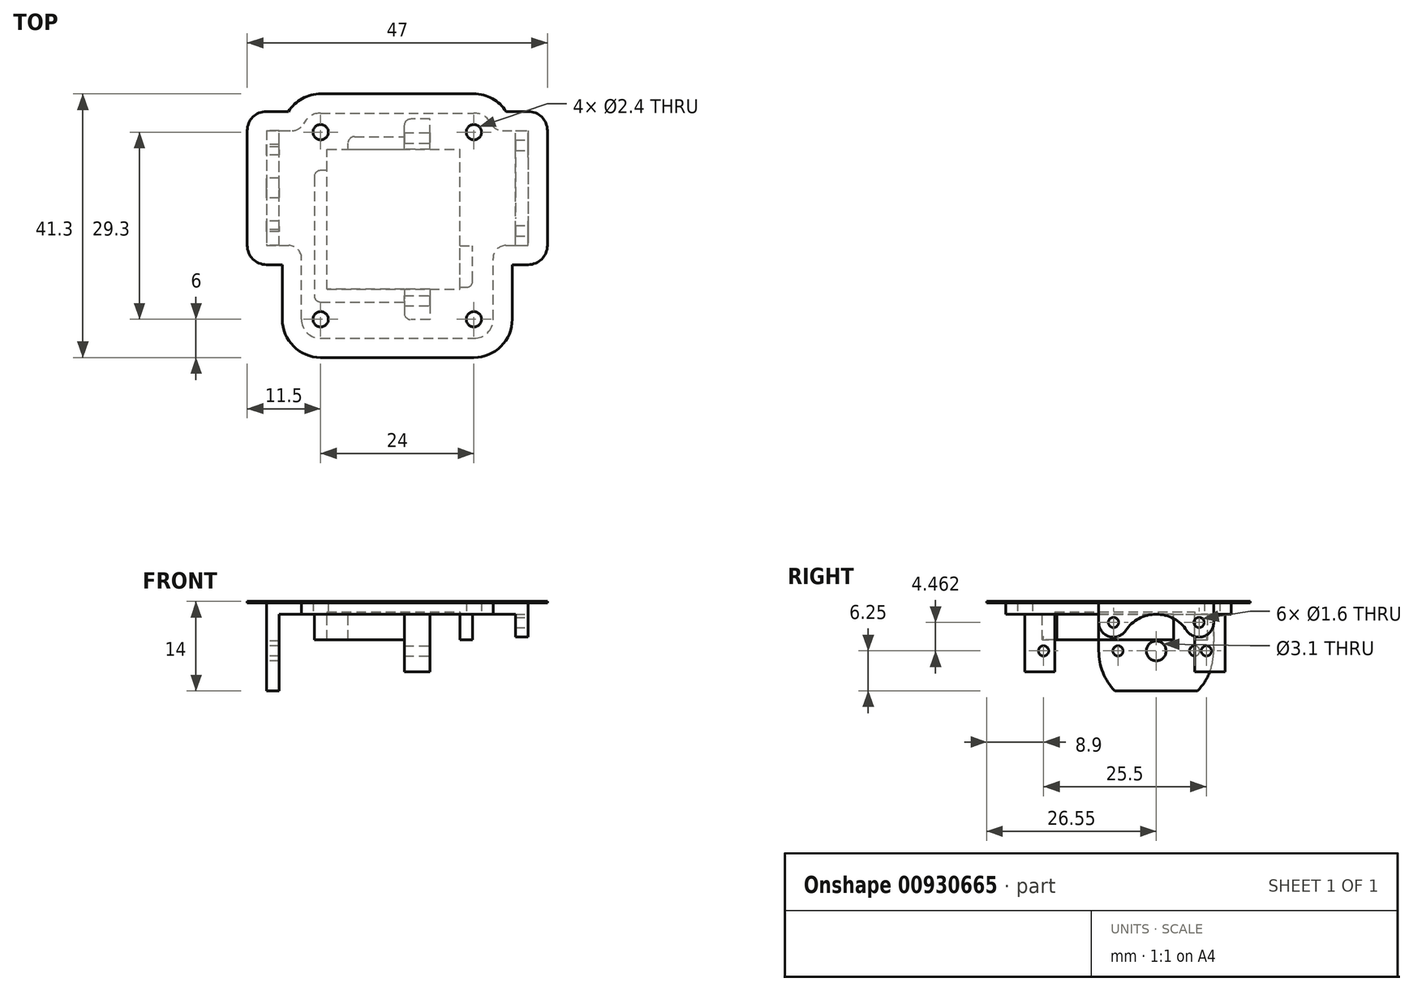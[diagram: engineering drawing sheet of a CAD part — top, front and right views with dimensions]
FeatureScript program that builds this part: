
annotation { "Feature Type Name" : "Feature", "Feature Type Description" : "" }
export const myFeature = defineFeature(function(context is Context, id is Id, definition is map)
    precondition{}
    {
        {
            var Q0;
            Q0=qCreatedBy(makeId("Top.planeOp"),FACE);
            var sketch = newSketch(context, id + "F0", { "sketchPlane" : qUnion([Q0])});
            skLineSegment(sketch, "E0.bottom", {"start": v(0, 0) * mm, "end": v(15.8, 0) * mm, "construction": true});
            skLineSegment(sketch, "E0.top", {"start": v(3, 21.3) * mm, "end": v(15.8, 21.3) * mm, "construction": true});
            skLineSegment(sketch, "E0.left", {"start": v(0, 0) * mm, "end": v(0, 18.3) * mm, "construction": true});
            skLineSegment(sketch, "E0.right", {"start": v(20.2, 0) * mm, "end": v(20.2, 21.3) * mm, "construction": true});
            skLineSegment(sketch, "E1.bottom", {"start": v(16.5, 25.35) * mm, "end": v(15.8, 25.35) * mm, "construction": true});
            skLineSegment(sketch, "E1.top", {"start": v(16.5, -4.05) * mm, "end": v(15.8, -4.05) * mm, "construction": true});
            skLineSegment(sketch, "E1.left", {"start": v(16.5, 25.35) * mm, "end": v(16.5, 21.3) * mm, "construction": true});
            skLineSegment(sketch, "E1.right", {"start": v(15.8, 25.35) * mm, "end": v(15.8, 21.3) * mm, "construction": true});
            skLineSegment(sketch, "E2.trimOffspring", {"start": v(16.5, 21.3) * mm, "end": v(20.2, 21.3) * mm, "construction": true});
            skLineSegment(sketch, "E3.trimOffspring", {"start": v(15.8, 0) * mm, "end": v(15.8, -4.05) * mm, "construction": true});
            skLineSegment(sketch, "E4.trimOffspring", {"start": v(16.5, 0) * mm, "end": v(16.5, -4.05) * mm, "construction": true});
            skLineSegment(sketch, "E5.trimOffspring", {"start": v(16.5, 0) * mm, "end": v(20.2, 0) * mm, "construction": true});
            skLineSegment(sketch, "E6", {"start": v(15.8, 23.4) * mm, "end": v(16.5, 23.4) * mm, "construction": true});
            skLineSegment(sketch, "E7", {"start": v(15.8, -2.1) * mm, "end": v(16.5, -2.1) * mm, "construction": true});
            skLineSegment(sketch, "E8", {"start": v(0, 18.3) * mm, "end": v(3, 21.3) * mm, "construction": true});
            skPoint(sketch, "E9.orphan", {"position": v(0, 21.3) * mm});
            skLineSegment(sketch, "E10", {"start": v(20.2, 21.3) * mm, "end": v(24.2, 21.3) * mm, "construction": true});
            skLineSegment(sketch, "E11", {"start": v(24.2, 21.3) * mm, "end": v(24.2, 6.8) * mm, "construction": true});
            skLineSegment(sketch, "E12", {"start": v(24.2, 6.8) * mm, "end": v(20.2, 6.8) * mm, "construction": true});
            skLineSegment(sketch, "E13", {"start": v(24.2, 15.55) * mm, "end": v(28.7, 15.55) * mm, "construction": true});
            skLineSegment(sketch, "E14.bottom", {"start": v(28.7, 21.3) * mm, "end": v(26.7, 21.3) * mm, "construction": true});
            skLineSegment(sketch, "E14.top", {"start": v(28.7, 0) * mm, "end": v(26.7, 0) * mm, "construction": true});
            skLineSegment(sketch, "E14.left", {"start": v(28.7, 21.3) * mm, "end": v(28.7, 0) * mm, "construction": true});
            skLineSegment(sketch, "E14.right", {"start": v(26.7, 21.3) * mm, "end": v(26.7, 0) * mm, "construction": true});
            skLineSegment(sketch, "E15.bottom", {"start": v(-7.3, 21.3) * mm, "end": v(-5.3, 21.3) * mm, "construction": true});
            skLineSegment(sketch, "E15.top", {"start": v(-7.3, 0) * mm, "end": v(-5.3, 0) * mm, "construction": true});
            skLineSegment(sketch, "E15.left", {"start": v(-7.3, 21.3) * mm, "end": v(-7.3, 0) * mm, "construction": true});
            skLineSegment(sketch, "E15.right", {"start": v(-5.3, 21.3) * mm, "end": v(-5.3, 0) * mm, "construction": true});
            skLineSegment(sketch, "E16", {"start": v(24.2, 18.55) * mm, "end": v(26.7, 18.55) * mm, "construction": true});
            skLineSegment(sketch, "E17", {"start": v(24.2, 12.55) * mm, "end": v(26.7, 12.55) * mm, "construction": true});
            skSolve(sketch);
        }
        {
            var Q0;
            Q0=qCreatedBy(makeId("Top.planeOp"),FACE);
            var sketch = newSketch(context, id + "F1", { "sketchPlane" : qUnion([Q0])});
            skLineSegment(sketch, "E18.left", {"start": v(-9.8, 24.55) * mm, "end": v(-9.8, 6.55) * mm});
            skLineSegment(sketch, "E18.right", {"start": v(31.2, 24.55) * mm, "end": v(31.2, 6.55) * mm});
            skLineSegment(sketch, "E19", {"start": v(10.7, 27.3) * mm, "end": v(10.7, -8) * mm, "construction": true});
            skCircle(sketch, "E20", {"center": v(-1.3, 24.3) * mm, "radius": 1.2 * mm});
            skCircle(sketch, "E21", {"center": v(22.7, 24.3) * mm, "radius": 1.2 * mm});
            skCircle(sketch, "E22", {"center": v(-1.3, -5) * mm, "radius": 1.2 * mm});
            skCircle(sketch, "E23", {"center": v(22.7, -5) * mm, "radius": 1.2 * mm});
            skLineSegment(sketch, "E24", {"start": v(-1.3, 24.3) * mm, "end": v(22.7, 24.3) * mm, "construction": true});
            skLineSegment(sketch, "E25", {"start": v(-1.3, 24.3) * mm, "end": v(-1.3, -5) * mm, "construction": true});
            skLineSegment(sketch, "E26", {"start": v(-1.3, -5) * mm, "end": v(22.7, -5) * mm, "construction": true});
            skLineSegment(sketch, "E27", {"start": v(22.7, -5) * mm, "end": v(22.7, 24.3) * mm, "construction": true});
            skArc(sketch, "E28", {"start": v(-1.3, 27.3) * mm, "mid": v(-3.33, 26.5) * mm, "end": v(-4.29, 24.55) * mm});
            skArc(sketch, "E29", {"start": v(25.69, 24.55) * mm, "mid": v(24.73, 26.5) * mm, "end": v(22.7, 27.3) * mm});
            skArc(sketch, "E30", {"start": v(-4.3, -5) * mm, "mid": v(-3.42, -7.12) * mm, "end": v(-1.3, -8) * mm});
            skArc(sketch, "E31", {"start": v(22.7, -8) * mm, "mid": v(24.82, -7.12) * mm, "end": v(25.7, -5) * mm});
            skLineSegment(sketch, "E32", {"start": v(-1.3, 27.3) * mm, "end": v(22.7, 27.3) * mm});
            skLineSegment(sketch, "E33", {"start": v(-4.3, -5) * mm, "end": v(-4.3, 6.55) * mm});
            skLineSegment(sketch, "E34", {"start": v(25.7, -5) * mm, "end": v(25.7, 6.55) * mm});
            skLineSegment(sketch, "E35", {"start": v(-1.3, -8) * mm, "end": v(22.7, -8) * mm});
            skLineSegment(sketch, "E36", {"start": v(-9.8, 24.55) * mm, "end": v(-4.29, 24.55) * mm});
            skLineSegment(sketch, "E37", {"start": v(25.69, 24.55) * mm, "end": v(31.2, 24.55) * mm});
            skLineSegment(sketch, "E38", {"start": v(-9.8, 6.55) * mm, "end": v(-4.3, 6.55) * mm});
            skLineSegment(sketch, "E39", {"start": v(25.7, 6.55) * mm, "end": v(31.2, 6.55) * mm});
            skSolve(sketch);
        }
        {
            var Q0;
            Q0=qSketchRegion(id+"F1",true);
            extrude(context, id + "F2", {"entities" : qUnion([Q0]), "depth" : 2 * mm, "offsetDistance" : 25 * mm});
        }
        {
            var Q0;
            Q0=makeQuery(id+"F2.opExtrude","SWEPT_EDGE",EDGE,{"disambiguationData":[OSD([sQuery(id+"F1.wireOp",EDGE,"E18.bottom"),sQuery(id+"F1.wireOp",EDGE,"n9spz6sa-SeqF-ro3C-UlOU-JdgqFO8XuwJj")])]});
            var Q1;
            Q1=makeQuery(id+"F2.opExtrude","SWEPT_EDGE",EDGE,{"disambiguationData":[OSD([sQuery(id+"F1.wireOp",EDGE,"v9wraEXt-J1L3-XLAm-fg3X-uzmLA6GDD1Q5"),sQuery(id+"F1.wireOp",EDGE,"3bf1b7fd-33ad-4c0a-b081-5d8ae0c3909f.trimOffspring")])]});
            var Q2;
            Q2=makeQuery(id+"F2.opExtrude","SWEPT_EDGE",EDGE,{"disambiguationData":[OSD([sQuery(id+"F1.wireOp",EDGE,"E34"),sQuery(id+"F1.wireOp",EDGE,"87065f72-439b-48f6-8dea-1321e7ddb749.trimOffspring")])]});
            var Q3;
            Q3=makeQuery(id+"F2.opExtrude","SWEPT_EDGE",EDGE,{"disambiguationData":[OSD([sQuery(id+"F1.wireOp",EDGE,"E18.top"),sQuery(id+"F1.wireOp",EDGE,"E33")])]});
            fillet(context, id + "F3", {"entities" : qUnion([Q0, Q1, Q2, Q3]), "radius" : 2 * mm, "tangentPropagation" : true, "allowEdgeOverflow" : false});
        }
        {
            var Q0;
            Q0=makeQuery(id+"F2.opExtrude","CAP_FACE",FACE,{"disambiguationData":[OSD([sQuery(id+"F1.wireOp",EDGE,"E18.bottom"),sQuery(id+"F1.wireOp",EDGE,"E18.top"),sQuery(id+"F1.wireOp",EDGE,"E18.left"),sQuery(id+"F1.wireOp",EDGE,"E18.right"),sQuery(id+"F1.wireOp",EDGE,"E20"),sQuery(id+"F1.wireOp",EDGE,"E21"),sQuery(id+"F1.wireOp",EDGE,"E22"),sQuery(id+"F1.wireOp",EDGE,"E23"),sQuery(id+"F1.wireOp",EDGE,"E28"),sQuery(id+"F1.wireOp",EDGE,"E29"),sQuery(id+"F1.wireOp",EDGE,"E30"),sQuery(id+"F1.wireOp",EDGE,"E31"),sQuery(id+"F1.wireOp",EDGE,"n9spz6sa-SeqF-ro3C-UlOU-JdgqFO8XuwJj"),sQuery(id+"F1.wireOp",EDGE,"E32"),sQuery(id+"F1.wireOp",EDGE,"v9wraEXt-J1L3-XLAm-fg3X-uzmLA6GDD1Q5"),sQuery(id+"F1.wireOp",EDGE,"E33"),sQuery(id+"F1.wireOp",EDGE,"E34"),sQuery(id+"F1.wireOp",EDGE,"E35"),sQuery(id+"F1.wireOp",EDGE,"3bf1b7fd-33ad-4c0a-b081-5d8ae0c3909f.trimOffspring"),sQuery(id+"F1.wireOp",EDGE,"87065f72-439b-48f6-8dea-1321e7ddb749.trimOffspring")])],"isStart":true});
            var sketch = newSketch(context, id + "F4", { "sketchPlane" : qUnion([Q0])});
            skLineSegment(sketch, "E40.bottom", {"start": v(15.8, 0.3) * mm, "end": v(11.8, 0.3) * mm});
            skLineSegment(sketch, "E40.top", {"start": v(15.8, 5.05) * mm, "end": v(11.8, 5.05) * mm});
            skLineSegment(sketch, "E40.left", {"start": v(15.8, 0.3) * mm, "end": v(15.8, 5.05) * mm});
            skLineSegment(sketch, "E40.right", {"start": v(11.8, 0.3) * mm, "end": v(11.8, 5.05) * mm});
            skLineSegment(sketch, "E41.bottom", {"start": v(15.8, -21.6) * mm, "end": v(11.8, -21.6) * mm});
            skLineSegment(sketch, "E41.top", {"start": v(15.8, -26.35) * mm, "end": v(11.8, -26.35) * mm});
            skLineSegment(sketch, "E41.left", {"start": v(15.8, -21.6) * mm, "end": v(15.8, -26.35) * mm});
            skLineSegment(sketch, "E41.right", {"start": v(11.8, -21.6) * mm, "end": v(11.8, -26.35) * mm});
            skSolve(sketch);
        }
        {
            var Q0;
            Q0=qSketchRegion(id+"F4",true);
            extrude(context, id + "F5", {"entities" : qUnion([Q0]), "operationType" : NewBodyOperationType.ADD, "depth" : 9 * mm, "offsetDistance" : 25 * mm});
        }
        {
            var Q0;
            Q0=makeQuery(id+"F2.opExtrude","CAP_FACE",FACE,{"disambiguationData":[OSD([sQuery(id+"F1.wireOp",EDGE,"E18.bottom"),sQuery(id+"F1.wireOp",EDGE,"E18.top"),sQuery(id+"F1.wireOp",EDGE,"E18.left"),sQuery(id+"F1.wireOp",EDGE,"E18.right"),sQuery(id+"F1.wireOp",EDGE,"E20"),sQuery(id+"F1.wireOp",EDGE,"E21"),sQuery(id+"F1.wireOp",EDGE,"E22"),sQuery(id+"F1.wireOp",EDGE,"E23"),sQuery(id+"F1.wireOp",EDGE,"E28"),sQuery(id+"F1.wireOp",EDGE,"E29"),sQuery(id+"F1.wireOp",EDGE,"E30"),sQuery(id+"F1.wireOp",EDGE,"E31"),sQuery(id+"F1.wireOp",EDGE,"n9spz6sa-SeqF-ro3C-UlOU-JdgqFO8XuwJj"),sQuery(id+"F1.wireOp",EDGE,"E32"),sQuery(id+"F1.wireOp",EDGE,"v9wraEXt-J1L3-XLAm-fg3X-uzmLA6GDD1Q5"),sQuery(id+"F1.wireOp",EDGE,"E33"),sQuery(id+"F1.wireOp",EDGE,"E34"),sQuery(id+"F1.wireOp",EDGE,"E35"),sQuery(id+"F1.wireOp",EDGE,"3bf1b7fd-33ad-4c0a-b081-5d8ae0c3909f.trimOffspring"),sQuery(id+"F1.wireOp",EDGE,"87065f72-439b-48f6-8dea-1321e7ddb749.trimOffspring")])],"isStart":true});
            var sketch = newSketch(context, id + "F6", { "sketchPlane" : qUnion([Q0])});
            skLineSegment(sketch, "E42", {"start": v(-0.3, -18.3) * mm, "end": v(-2.3, -18.3) * mm});
            skLineSegment(sketch, "E43", {"start": v(-2.3, -18.3) * mm, "end": v(-2.3, 2.3) * mm});
            skLineSegment(sketch, "E44", {"start": v(-2.3, 2.3) * mm, "end": v(11.8, 2.3) * mm});
            skLineSegment(sketch, "E45", {"start": v(11.8, 2.3) * mm, "end": v(11.8, 0.3) * mm});
            skLineSegment(sketch, "E46", {"start": v(11.8, 0.3) * mm, "end": v(-0.3, 0.3) * mm});
            skLineSegment(sketch, "E47", {"start": v(-0.3, 0.3) * mm, "end": v(-0.3, -18.3) * mm});
            skLineSegment(sketch, "E48.bottom", {"start": v(3, -21.6) * mm, "end": v(11.8, -21.6) * mm});
            skLineSegment(sketch, "E48.top", {"start": v(3, -23.6) * mm, "end": v(11.8, -23.6) * mm});
            skLineSegment(sketch, "E48.left", {"start": v(3, -21.6) * mm, "end": v(3, -23.6) * mm});
            skLineSegment(sketch, "E48.right", {"start": v(11.8, -21.6) * mm, "end": v(11.8, -23.6) * mm});
            skLineSegment(sketch, "E49.bottom", {"start": v(20.5, 0) * mm, "end": v(22.5, 0) * mm});
            skLineSegment(sketch, "E49.top", {"start": v(20.5, -6.5) * mm, "end": v(22.5, -6.5) * mm});
            skLineSegment(sketch, "E49.left", {"start": v(20.5, 0) * mm, "end": v(20.5, -6.5) * mm});
            skLineSegment(sketch, "E49.right", {"start": v(22.5, 0) * mm, "end": v(22.5, -6.5) * mm});
            skSolve(sketch);
        }
        {
            var Q0;
            Q0=qSketchRegion(id+"F6",true);
            extrude(context, id + "F7", {"entities" : qUnion([Q0]), "operationType" : NewBodyOperationType.ADD, "depth" : 4 * mm, "offsetDistance" : 25 * mm});
        }
        {
            var Q0;
            Q0=makeQuery(id+"F5.opExtrude","SWEPT_FACE",FACE,{"disambiguationData":[OSD([sQuery(id+"F4.wireOp",EDGE,"E41.left")])]});
            var sketch = newSketch(context, id + "F8", { "sketchPlane" : qUnion([Q0])});
            skCircle(sketch, "E50", {"center": v(23.4, -5.75) * mm, "radius": 0.8 * mm});
            skCircle(sketch, "E51", {"center": v(-2.1, -5.75) * mm, "radius": 0.8 * mm});
            skSolve(sketch);
        }
        {
            var Q0;
            Q0=qSketchRegion(id+"F8",true);
            extrude(context, id + "F9", {"entities" : qUnion([Q0]), "operationType" : NewBodyOperationType.REMOVE, "endBound" : BoundingType.UP_TO_NEXT, "oppositeDirection" : true, "depth" : 25 * mm, "offsetDistance" : 25 * mm});
        }
        {
            var Q0;
            Q0=makeQuery(id+"F7.opExtrude","CAP_EDGE",EDGE,{"disambiguationData":[OSD([sQuery(id+"F6.wireOp",EDGE,"E45")])],"isStart":false});
            var Q1;
            Q1=makeQuery(id+"F7.opExtrude","SWEPT_EDGE",EDGE,{"disambiguationData":[OSD([sQuery(id+"F4.wireOp",EDGE,"E40.right"),sQuery(id+"F6.wireOp",EDGE,"E44"),sQuery(id+"F6.wireOp",EDGE,"E45")])]});
            var Q2;
            Q2=makeQuery(id+"F7.opExtrude","SWEPT_EDGE",EDGE,{"disambiguationData":[OSD([sQuery(id+"F6.wireOp",EDGE,"E43"),sQuery(id+"F6.wireOp",EDGE,"E44")])]});
            var Q3;
            Q3=makeQuery(id+"F7.opExtrude","SWEPT_EDGE",EDGE,{"disambiguationData":[OSD([sQuery(id+"F6.wireOp",EDGE,"E42"),sQuery(id+"F6.wireOp",EDGE,"E43")])]});
            var Q4;
            Q4=makeQuery(id+"F7.opExtrude","SWEPT_EDGE",EDGE,{"disambiguationData":[OSD([sQuery(id+"F6.wireOp",EDGE,"E48.top"),sQuery(id+"F6.wireOp",EDGE,"E48.left")])]});
            var Q5;
            Q5=makeQuery(id+"F7.opExtrude","SWEPT_EDGE",EDGE,{"disambiguationData":[OSD([sQuery(id+"F4.wireOp",EDGE,"E41.right"),sQuery(id+"F6.wireOp",EDGE,"E48.top"),sQuery(id+"F6.wireOp",EDGE,"E48.right")])]});
            var Q6;
            Q6=makeQuery(id+"F7.opExtrude","CAP_EDGE",EDGE,{"disambiguationData":[OSD([sQuery(id+"F6.wireOp",EDGE,"E48.right")])],"isStart":false});
            var Q7;
            Q7=makeQuery(id+"F7.opExtrude","SWEPT_EDGE",EDGE,{"disambiguationData":[OSD([sQuery(id+"F6.wireOp",EDGE,"E49.bottom"),sQuery(id+"F6.wireOp",EDGE,"E49.right")])]});
            var Q8;
            Q8=makeQuery(id+"F5.opExtrude","SWEPT_EDGE",EDGE,{"disambiguationData":[OSD([sQuery(id+"F4.wireOp",EDGE,"E41.top"),sQuery(id+"F4.wireOp",EDGE,"E41.right")])]});
            var Q9;
            Q9=makeQuery(id+"F5.opExtrude","SWEPT_EDGE",EDGE,{"disambiguationData":[OSD([sQuery(id+"F4.wireOp",EDGE,"E40.top"),sQuery(id+"F4.wireOp",EDGE,"E40.right")])]});
            fillet(context, id + "F10", {"entities" : qUnion([Q0, Q1, Q2, Q3, Q4, Q5, Q6, Q7, Q8, Q9]), "radius" : 1 * mm, "tangentPropagation" : true, "allowEdgeOverflow" : false});
        }
        {
            var Q0;
            Q0=makeQuery(id+"F2.opExtrude","CAP_FACE",FACE,{"disambiguationData":[OSD([sQuery(id+"F1.wireOp",EDGE,"E18.bottom"),sQuery(id+"F1.wireOp",EDGE,"E18.top"),sQuery(id+"F1.wireOp",EDGE,"E18.left"),sQuery(id+"F1.wireOp",EDGE,"E18.right"),sQuery(id+"F1.wireOp",EDGE,"E20"),sQuery(id+"F1.wireOp",EDGE,"E21"),sQuery(id+"F1.wireOp",EDGE,"E22"),sQuery(id+"F1.wireOp",EDGE,"E23"),sQuery(id+"F1.wireOp",EDGE,"E28"),sQuery(id+"F1.wireOp",EDGE,"E29"),sQuery(id+"F1.wireOp",EDGE,"E30"),sQuery(id+"F1.wireOp",EDGE,"E31"),sQuery(id+"F1.wireOp",EDGE,"n9spz6sa-SeqF-ro3C-UlOU-JdgqFO8XuwJj"),sQuery(id+"F1.wireOp",EDGE,"E32"),sQuery(id+"F1.wireOp",EDGE,"v9wraEXt-J1L3-XLAm-fg3X-uzmLA6GDD1Q5"),sQuery(id+"F1.wireOp",EDGE,"E33"),sQuery(id+"F1.wireOp",EDGE,"E34"),sQuery(id+"F1.wireOp",EDGE,"E35"),sQuery(id+"F1.wireOp",EDGE,"3bf1b7fd-33ad-4c0a-b081-5d8ae0c3909f.trimOffspring"),sQuery(id+"F1.wireOp",EDGE,"87065f72-439b-48f6-8dea-1321e7ddb749.trimOffspring")])],"isStart":true});
            var sketch = newSketch(context, id + "F11", { "sketchPlane" : qUnion([Q0])});
            skLineSegment(sketch, "E52.bottom", {"start": v(-9.8, -6.55) * mm, "end": v(-7.8, -6.55) * mm});
            skLineSegment(sketch, "E52.top", {"start": v(-9.8, -24.55) * mm, "end": v(-7.8, -24.55) * mm});
            skLineSegment(sketch, "E52.left", {"start": v(-9.8, -6.55) * mm, "end": v(-9.8, -24.55) * mm});
            skLineSegment(sketch, "E52.right", {"start": v(-7.8, -6.55) * mm, "end": v(-7.8, -24.55) * mm});
            skLineSegment(sketch, "E53.bottom", {"start": v(31.2, -6.55) * mm, "end": v(29.2, -6.55) * mm});
            skLineSegment(sketch, "E53.top", {"start": v(31.2, -24.55) * mm, "end": v(29.2, -24.55) * mm});
            skLineSegment(sketch, "E53.left", {"start": v(31.2, -6.55) * mm, "end": v(31.2, -24.55) * mm});
            skLineSegment(sketch, "E53.right", {"start": v(29.2, -6.55) * mm, "end": v(29.2, -24.55) * mm});
            skSolve(sketch);
        }
        {
            var Q0;
            Q0=qSketchRegion(id+"F11",true);
            extrude(context, id + "F12", {"entities" : qUnion([Q0]), "operationType" : NewBodyOperationType.ADD, "depth" : 12 * mm, "offsetDistance" : 25 * mm});
        }
        {
            var Q0;
            Q0=makeQuery(id+"F12.boolean.opBoolean","MERGE",FACE,{"derivedFrom":[makeQuery(id+"F2.opExtrude","SWEPT_FACE",FACE,{"disambiguationData":[OSD([sQuery(id+"F1.wireOp",EDGE,"E18.left")])]}),makeQuery(id+"F12.opExtrude","SWEPT_FACE",FACE,{"disambiguationData":[OSD([sQuery(id+"F11.wireOp",EDGE,"E52.left")])]})]});
            var sketch = newSketch(context, id + "F13", { "sketchPlane" : qUnion([Q0])});
            skCircle(sketch, "E54", {"center": v(-15.55, -5.75) * mm, "radius": 1.55 * mm});
            skLineSegment(sketch, "E55", {"start": v(-24.55, -5.75) * mm, "end": v(-6.55, -5.75) * mm, "construction": true});
            skCircle(sketch, "E56", {"center": v(-21.55, -5.75) * mm, "radius": 0.8 * mm});
            skCircle(sketch, "E57", {"center": v(-9.55, -5.75) * mm, "radius": 0.8 * mm});
            skArc(sketch, "E58", {"start": v(-24.55, -5.75) * mm, "mid": v(-23.9, -9.12) * mm, "end": v(-22.03, -12) * mm});
            skArc(sketch, "E59", {"start": v(-9.07, -12) * mm, "mid": v(-7.2, -9.12) * mm, "end": v(-6.55, -5.75) * mm});
            skLineSegment(sketch, "E60", {"start": v(-24.55, -5.75) * mm, "end": v(-24.55, -12) * mm});
            skLineSegment(sketch, "E61", {"start": v(-24.55, -12) * mm, "end": v(-22.03, -12) * mm});
            skLineSegment(sketch, "E62", {"start": v(-9.07, -12) * mm, "end": v(-6.55, -12) * mm});
            skLineSegment(sketch, "E63", {"start": v(-6.55, -12) * mm, "end": v(-6.55, -5.75) * mm});
            skSolve(sketch);
        }
        {
            var Q0;
            Q0=qSketchRegion(id+"F13",true);
            extrude(context, id + "F14", {"entities" : qUnion([Q0]), "operationType" : NewBodyOperationType.REMOVE, "endBound" : BoundingType.UP_TO_NEXT, "oppositeDirection" : true, "depth" : 25 * mm, "offsetDistance" : 25 * mm});
        }
        {
            var Q0;
            Q0=makeQuery(id+"F12.boolean.opBoolean","MERGE",FACE,{"derivedFrom":[makeQuery(id+"F2.opExtrude","SWEPT_FACE",FACE,{"disambiguationData":[OSD([sQuery(id+"F1.wireOp",EDGE,"E18.right")])]}),makeQuery(id+"F12.opExtrude","SWEPT_FACE",FACE,{"disambiguationData":[OSD([sQuery(id+"F11.wireOp",EDGE,"E53.left")])]})]});
            var sketch = newSketch(context, id + "F15", { "sketchPlane" : qUnion([Q0])});
            skCircle(sketch, "E64", {"center": v(15.55, -5.75) * mm, "radius": 5.5 * mm, "construction": true});
            skLineSegment(sketch, "E65", {"start": v(6.55, -5.75) * mm, "end": v(24.55, -5.75) * mm, "construction": true});
            skArc(sketch, "E66", {"start": v(20.34, -2.56) * mm, "mid": v(15.55, 0) * mm, "end": v(10.76, -2.56) * mm});
            skArc(sketch, "E67", {"start": v(11.05, -2.59) * mm, "mid": v(8.73, -6.04) * mm, "end": v(6.55, -9.6) * mm, "construction": true});
            skCircle(sketch, "E68", {"center": v(8.85, -1.29) * mm, "radius": 0.8 * mm});
            skArc(sketch, "E69", {"start": v(20.37, -8.4) * mm, "mid": v(19.48, -10.17) * mm, "end": v(18.74, -12) * mm, "construction": true});
            skCircle(sketch, "E70", {"center": v(22.25, -1.29) * mm, "radius": 0.8 * mm});
            skLineSegment(sketch, "E71", {"start": v(6.55, -12) * mm, "end": v(24.55, -12) * mm});
            skArc(sketch, "E72", {"start": v(6.55, -1.29) * mm, "mid": v(8.18, -3.49) * mm, "end": v(10.76, -2.56) * mm});
            skLineSegment(sketch, "E73", {"start": v(6.55, -1.29) * mm, "end": v(6.55, -12) * mm});
            skArc(sketch, "E74", {"start": v(20.34, -2.56) * mm, "mid": v(22.92, -3.49) * mm, "end": v(24.55, -1.29) * mm});
            skLineSegment(sketch, "E75", {"start": v(24.55, -1.29) * mm, "end": v(24.55, -12) * mm});
            skSolve(sketch);
        }
        {
            var Q0;
            Q0=qSketchRegion(id+"F15",true);
            extrude(context, id + "F16", {"entities" : qUnion([Q0]), "operationType" : NewBodyOperationType.REMOVE, "endBound" : BoundingType.UP_TO_NEXT, "oppositeDirection" : true, "depth" : 25 * mm, "offsetDistance" : 25 * mm});
        }
        {
            var Q0;
            Q0=makeQuery(id+"F2.opExtrude","SWEPT_EDGE",EDGE,{"disambiguationData":[OSD([sQuery(id+"F1.wireOp",EDGE,"E28"),sQuery(id+"F1.wireOp",EDGE,"E36")])]});
            var Q1;
            Q1=makeQuery(id+"F2.opExtrude","SWEPT_EDGE",EDGE,{"disambiguationData":[OSD([sQuery(id+"F1.wireOp",EDGE,"E29"),sQuery(id+"F1.wireOp",EDGE,"E37")])]});
            fillet(context, id + "F17", {"entities" : qUnion([Q0, Q1]), "radius" : 2 * mm, "tangentPropagation" : true, "allowEdgeOverflow" : false});
        }
        {
            var Q0;
            Q0=makeQuery(id+"F2.opExtrude","CAP_FACE",FACE,{"disambiguationData":[OSD([sQuery(id+"F1.wireOp",EDGE,"E18.left"),sQuery(id+"F1.wireOp",EDGE,"E18.right"),sQuery(id+"F1.wireOp",EDGE,"E20"),sQuery(id+"F1.wireOp",EDGE,"E21"),sQuery(id+"F1.wireOp",EDGE,"E22"),sQuery(id+"F1.wireOp",EDGE,"E23"),sQuery(id+"F1.wireOp",EDGE,"E28"),sQuery(id+"F1.wireOp",EDGE,"E29"),sQuery(id+"F1.wireOp",EDGE,"E30"),sQuery(id+"F1.wireOp",EDGE,"E31"),sQuery(id+"F1.wireOp",EDGE,"E32"),sQuery(id+"F1.wireOp",EDGE,"E33"),sQuery(id+"F1.wireOp",EDGE,"E34"),sQuery(id+"F1.wireOp",EDGE,"E35"),sQuery(id+"F1.wireOp",EDGE,"E36"),sQuery(id+"F1.wireOp",EDGE,"E37"),sQuery(id+"F1.wireOp",EDGE,"E38"),sQuery(id+"F1.wireOp",EDGE,"E39")])],"isStart":false});
            var sketch = newSketch(context, id + "F18", { "sketchPlane" : qUnion([Q0])});
            skLineSegment(sketch, "E76", {"start": v(-9.8, 24.55) * mm, "end": v(-9.8, 6.55) * mm});
            skLineSegment(sketch, "E77", {"start": v(-9.8, 6.55) * mm, "end": v(-6.3, 6.55) * mm});
            skLineSegment(sketch, "E78", {"start": v(-5.77, 24.55) * mm, "end": v(-9.8, 24.55) * mm});
            skLineSegment(sketch, "E79", {"start": v(-1.3, 27.3) * mm, "end": v(22.7, 27.3) * mm});
            skLineSegment(sketch, "E80", {"start": v(27.17, 24.55) * mm, "end": v(31.2, 24.55) * mm});
            skLineSegment(sketch, "E81", {"start": v(31.2, 24.55) * mm, "end": v(31.2, 6.55) * mm});
            skLineSegment(sketch, "E82", {"start": v(31.2, 6.55) * mm, "end": v(27.7, 6.55) * mm});
            skLineSegment(sketch, "E83", {"start": v(-4.3, 4.55) * mm, "end": v(-4.3, -5) * mm});
            skLineSegment(sketch, "E84", {"start": v(-1.3, -8) * mm, "end": v(22.7, -8) * mm});
            skLineSegment(sketch, "E85", {"start": v(25.7, 4.55) * mm, "end": v(25.7, -5) * mm});
            skArc(sketch, "E86", {"start": v(-4.3, 4.55) * mm, "mid": v(-4.89, 5.96) * mm, "end": v(-6.3, 6.55) * mm});
            skArc(sketch, "E87", {"start": v(27.7, 6.55) * mm, "mid": v(26.29, 5.96) * mm, "end": v(25.7, 4.55) * mm});
            skArc(sketch, "E88", {"start": v(22.7, -8) * mm, "mid": v(24.82, -7.12) * mm, "end": v(25.7, -5) * mm});
            skArc(sketch, "E89", {"start": v(-4.3, -5) * mm, "mid": v(-3.42, -7.12) * mm, "end": v(-1.3, -8) * mm});
            skArc(sketch, "E90", {"start": v(-5.77, 24.55) * mm, "mid": v(-4.72, 24.85) * mm, "end": v(-3.98, 25.65) * mm});
            skArc(sketch, "E91", {"start": v(-1.3, 27.3) * mm, "mid": v(-2.87, 26.85) * mm, "end": v(-3.98, 25.65) * mm});
            skArc(sketch, "E92", {"start": v(25.38, 25.65) * mm, "mid": v(24.27, 26.85) * mm, "end": v(22.7, 27.3) * mm});
            skArc(sketch, "E93", {"start": v(25.38, 25.65) * mm, "mid": v(26.12, 24.85) * mm, "end": v(27.17, 24.55) * mm});
            skLineSegment(sketch, "E94", {"start": v(-12.8, 24.55) * mm, "end": v(-12.8, 6.55) * mm});
            skLineSegment(sketch, "E95", {"start": v(-7.3, 3.55) * mm, "end": v(-7.3, -5) * mm});
            skLineSegment(sketch, "E96", {"start": v(-7.3, 3.55) * mm, "end": v(-9.8, 3.55) * mm});
            skLineSegment(sketch, "E97", {"start": v(-9.8, 27.55) * mm, "end": v(-6.34, 27.55) * mm});
            skLineSegment(sketch, "E98", {"start": v(-1.3, 30.3) * mm, "end": v(22.7, 30.3) * mm});
            skArc(sketch, "E99", {"start": v(-9.8, 27.55) * mm, "mid": v(-11.92, 26.67) * mm, "end": v(-12.8, 24.55) * mm});
            skArc(sketch, "E100", {"start": v(-12.8, 6.55) * mm, "mid": v(-11.92, 4.43) * mm, "end": v(-9.8, 3.55) * mm});
            skArc(sketch, "E101", {"start": v(-1.3, 30.3) * mm, "mid": v(-4.17, 29.57) * mm, "end": v(-6.34, 27.55) * mm});
            skLineSegment(sketch, "E102", {"start": v(-1.3, -11) * mm, "end": v(22.7, -11) * mm});
            skLineSegment(sketch, "E103", {"start": v(28.7, 3.55) * mm, "end": v(28.7, -5) * mm});
            skLineSegment(sketch, "E104", {"start": v(28.7, 3.55) * mm, "end": v(31.2, 3.55) * mm});
            skLineSegment(sketch, "E105", {"start": v(34.2, 24.55) * mm, "end": v(34.2, 6.55) * mm});
            skLineSegment(sketch, "E106", {"start": v(27.74, 27.55) * mm, "end": v(31.2, 27.55) * mm});
            skArc(sketch, "E107", {"start": v(34.2, 24.55) * mm, "mid": v(33.32, 26.67) * mm, "end": v(31.2, 27.55) * mm});
            skArc(sketch, "E108", {"start": v(22.7, -11) * mm, "mid": v(26.94, -9.24) * mm, "end": v(28.7, -5) * mm});
            skArc(sketch, "E109", {"start": v(-7.3, -5) * mm, "mid": v(-5.54, -9.24) * mm, "end": v(-1.3, -11) * mm});
            skArc(sketch, "E110", {"start": v(27.74, 27.55) * mm, "mid": v(25.57, 29.57) * mm, "end": v(22.7, 30.3) * mm});
            skArc(sketch, "E111", {"start": v(31.2, 3.55) * mm, "mid": v(33.32, 4.43) * mm, "end": v(34.2, 6.55) * mm});
            skSolve(sketch);
        }
        {
            var Q0;
            Q0=qSketchRegion(id+"F18",true);
            extrude(context, id + "F19", {"entities" : qUnion([Q0]), "operationType" : NewBodyOperationType.ADD, "oppositeDirection" : true, "depth" : 0.2 * mm, "offsetDistance" : 25 * mm});
        }
        {
            var Q0;
            Q0=makeQuery(id+"F2.opExtrude","CAP_FACE",FACE,{"disambiguationData":[OSD([sQuery(id+"F1.wireOp",EDGE,"E18.left"),sQuery(id+"F1.wireOp",EDGE,"E18.right"),sQuery(id+"F1.wireOp",EDGE,"E20"),sQuery(id+"F1.wireOp",EDGE,"E21"),sQuery(id+"F1.wireOp",EDGE,"E22"),sQuery(id+"F1.wireOp",EDGE,"E23"),sQuery(id+"F1.wireOp",EDGE,"E28"),sQuery(id+"F1.wireOp",EDGE,"E29"),sQuery(id+"F1.wireOp",EDGE,"E30"),sQuery(id+"F1.wireOp",EDGE,"E31"),sQuery(id+"F1.wireOp",EDGE,"E32"),sQuery(id+"F1.wireOp",EDGE,"E33"),sQuery(id+"F1.wireOp",EDGE,"E34"),sQuery(id+"F1.wireOp",EDGE,"E35"),sQuery(id+"F1.wireOp",EDGE,"E36"),sQuery(id+"F1.wireOp",EDGE,"E37"),sQuery(id+"F1.wireOp",EDGE,"E38"),sQuery(id+"F1.wireOp",EDGE,"E39")])],"isStart":true});
            var sketch = newSketch(context, id + "F20", { "sketchPlane" : qUnion([Q0])});
            skLineSegment(sketch, "E112.bottom", {"start": v(-0.3, 0.3) * mm, "end": v(20.5, 0.3) * mm});
            skLineSegment(sketch, "E112.top", {"start": v(-0.3, -21.6) * mm, "end": v(20.5, -21.6) * mm});
            skLineSegment(sketch, "E112.left", {"start": v(-0.3, 0.3) * mm, "end": v(-0.3, -21.6) * mm});
            skLineSegment(sketch, "E112.right", {"start": v(20.5, 0.3) * mm, "end": v(20.5, -21.6) * mm});
            skSolve(sketch);
        }
        {
            var Q0;
            Q0=qSketchRegion(id+"F20",true);
            extrude(context, id + "F21", {"entities" : qUnion([Q0]), "operationType" : NewBodyOperationType.REMOVE, "oppositeDirection" : true, "depth" : 0.4 * mm, "offsetDistance" : 25 * mm});
        }
    });
